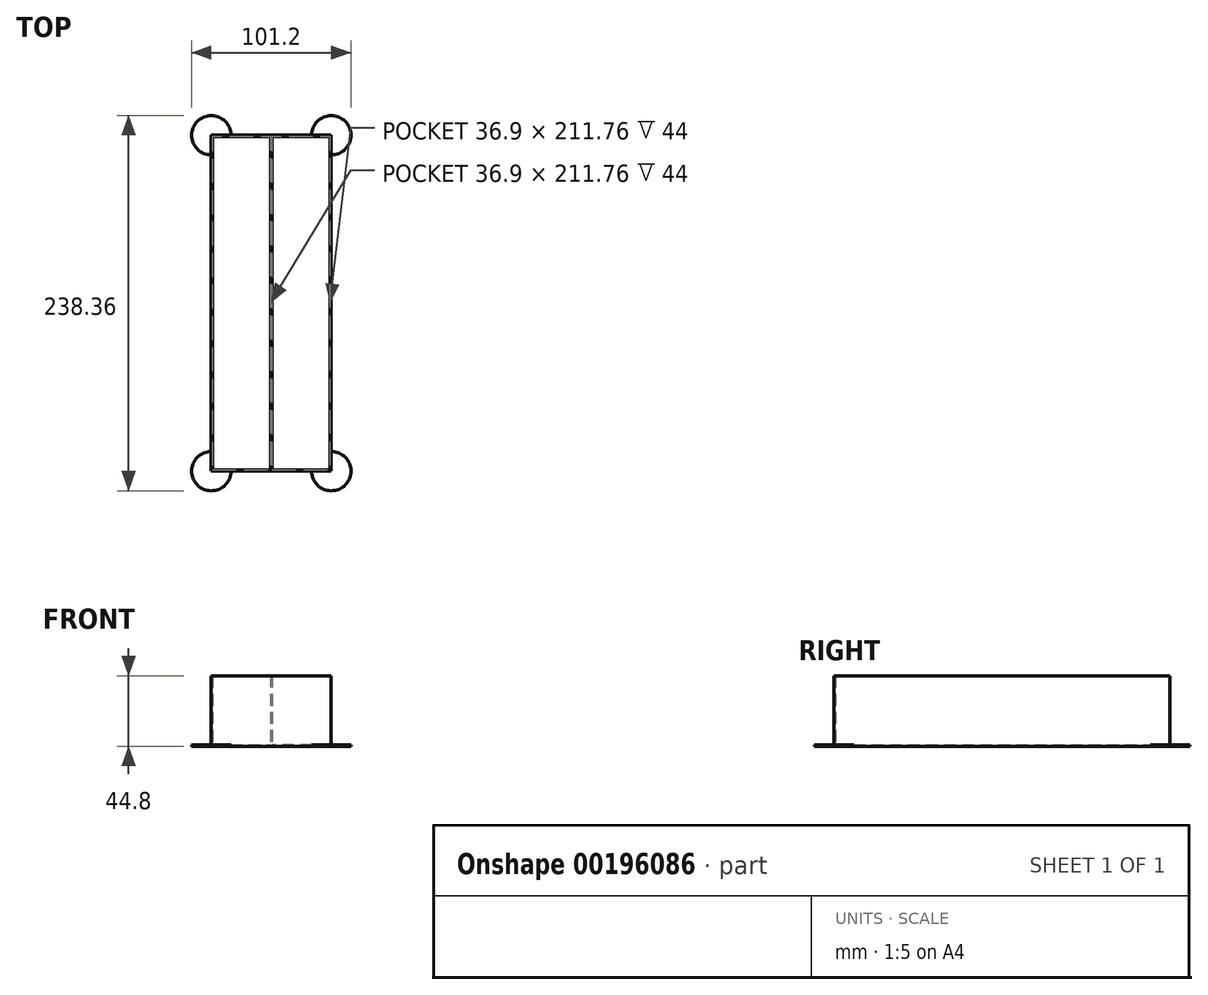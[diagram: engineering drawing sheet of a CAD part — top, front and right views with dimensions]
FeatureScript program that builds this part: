
annotation { "Feature Type Name" : "Feature", "Feature Type Description" : "" }
export const myFeature = defineFeature(function(context is Context, id is Id, definition is map)
    precondition{}
    {
        {
            var Q0;
            Q0=qCreatedBy(makeId("Top.planeOp"),FACE);
            var sketch = newSketch(context, id + "F0", { "sketchPlane" : qUnion([Q0])});
            skLineSegment(sketch, "E0.bottom", {"start": v(0, 0) * mm, "end": v(76.2, 0) * mm});
            skLineSegment(sketch, "E0.top", {"start": v(0, 213.36) * mm, "end": v(76.2, 213.36) * mm});
            skLineSegment(sketch, "E0.left", {"start": v(0, 0) * mm, "end": v(0, 213.36) * mm});
            skLineSegment(sketch, "E0.right", {"start": v(76.2, 0) * mm, "end": v(76.2, 213.36) * mm});
            skCircle(sketch, "E1", {"center": v(76.2, 0) * mm, "radius": 12.5 * mm});
            skCircle(sketch, "E2", {"center": v(0, 0) * mm, "radius": 12.5 * mm});
            skCircle(sketch, "E3", {"center": v(76.2, 213.36) * mm, "radius": 12.5 * mm});
            skCircle(sketch, "E4", {"center": v(0, 213.36) * mm, "radius": 12.5 * mm});
            skSolve(sketch);
        }
        {
            var Q0;
            Q0=makeQuery(id+"F0.imprint","IMPRINT",FACE,{"disambiguationData":[TD([[makeQuery(id+"F0.imprint","IMPRINT",EDGE,{"derivedFrom":sQuery(id+"F0.wireOp",EDGE,"E0.bottom")}),1.0]])]});
            var Q1;
            {var subQ5=sQuery(id+"F0.wireOp",EDGE,"E2");var subQ10=sQuery(id+"F0.wireOp",EDGE,"E0.bottom");var subQ11=makeQuery(id+"F0.imprint","INTERSECT",VERTEX,{"derivedFrom":[subQ10,subQ5]});Q1=makeQuery(id+"F0.imprint","IMPRINT",FACE,{"disambiguationData":[TD([[makeQuery(id+"F0.imprint","IMPRINT",EDGE,{"disambiguationData":[TD([[subQ11,-1.0]])],"derivedFrom":subQ10}),1.0]])]});}
            var Q2;
            {var subQ0=sQuery(id+"F0.wireOp",EDGE,"E0.right");var subQ1=sQuery(id+"F0.wireOp",EDGE,"E0.top");var subQ2=makeQuery(id+"F0.imprint","INTERSECT",VERTEX,{"derivedFrom":[subQ1,subQ0]});Q2=makeQuery(id+"F0.imprint","IMPRINT",FACE,{"disambiguationData":[TD([[makeQuery(id+"F0.imprint","IMPRINT",EDGE,{"disambiguationData":[TD([[subQ2,1.0]])],"derivedFrom":subQ1}),-1.0]])]});}
            var Q3;
            {var subQ0=sQuery(id+"F0.wireOp",EDGE,"E0.left");var subQ1=sQuery(id+"F0.wireOp",EDGE,"E0.top");var subQ2=makeQuery(id+"F0.imprint","INTERSECT",VERTEX,{"derivedFrom":[subQ1,subQ0]});Q3=makeQuery(id+"F0.imprint","IMPRINT",FACE,{"disambiguationData":[TD([[makeQuery(id+"F0.imprint","IMPRINT",EDGE,{"disambiguationData":[TD([[subQ2,-1.0]])],"derivedFrom":subQ1}),-1.0]])]});}
            extrude(context, id + "F1", {"entities" : qUnion([Q0, Q1, Q2, Q3]), "depth" : 0.8 * mm});
        }
        {
            var Q0;
            Q0=makeQuery(id+"F1.opExtrude","CAP_FACE",FACE,{"disambiguationData":[OSD([sQuery(id+"F0.wireOp",EDGE,"E0.bottom"),sQuery(id+"F0.wireOp",EDGE,"E0.top"),sQuery(id+"F0.wireOp",EDGE,"E0.left"),sQuery(id+"F0.wireOp",EDGE,"E0.right")])],"isStart":false});
            var sketch = newSketch(context, id + "F2", { "sketchPlane" : qUnion([Q0])});
            skLineSegment(sketch, "E5.0", {"start": v(0, 213.36) * mm, "end": v(76.2, 213.36) * mm});
            skLineSegment(sketch, "E5.1", {"start": v(0, 0) * mm, "end": v(0, 213.36) * mm});
            skLineSegment(sketch, "E5.2", {"start": v(76.2, 0) * mm, "end": v(76.2, 213.36) * mm});
            skLineSegment(sketch, "E5.3", {"start": v(0, 0) * mm, "end": v(76.2, 0) * mm});
            skLineSegment(sketch, "E6", {"start": v(38.1, 213.36) * mm, "end": v(38.1, 0) * mm, "construction": true});
            skLineSegment(sketch, "E7.bottom", {"start": v(0.8, 212.56) * mm, "end": v(37.7, 212.56) * mm});
            skLineSegment(sketch, "E7.top", {"start": v(0.8, 0.8) * mm, "end": v(37.7, 0.8) * mm});
            skLineSegment(sketch, "E7.left", {"start": v(0.8, 212.56) * mm, "end": v(0.8, 0.8) * mm});
            skLineSegment(sketch, "E7.right", {"start": v(37.7, 212.56) * mm, "end": v(37.7, 0.8) * mm});
            skLineSegment(sketch, "E8.bottom", {"start": v(75.4, 0.8) * mm, "end": v(38.5, 0.8) * mm});
            skLineSegment(sketch, "E8.top", {"start": v(75.4, 212.56) * mm, "end": v(38.5, 212.56) * mm});
            skLineSegment(sketch, "E8.left", {"start": v(75.4, 0.8) * mm, "end": v(75.4, 212.56) * mm});
            skLineSegment(sketch, "E8.right", {"start": v(38.5, 0.8) * mm, "end": v(38.5, 212.56) * mm});
            skSolve(sketch);
        }
        {
            var Q0;
            Q0 = qSketchRegion(id + "F2", true);
            extrude(context, id + "F3", {"entities" : qUnion([Q0]), "operationType" : NewBodyOperationType.ADD, "depth" : 44 * mm});
        }
        {
            var Q0;
            {var subQ0=sQuery(id+"F0.wireOp",EDGE,"E0.right");var subQ1=sQuery(id+"F0.wireOp",EDGE,"E0.bottom");var subQ2=makeQuery(id+"F0.imprint","INTERSECT",VERTEX,{"derivedFrom":[subQ1,subQ0]});Q0=makeQuery(id+"F0.imprint","IMPRINT",FACE,{"disambiguationData":[TD([[makeQuery(id+"F0.imprint","IMPRINT",EDGE,{"disambiguationData":[TD([[subQ2,1.0]])],"derivedFrom":subQ1}),-1.0]])]});}
            var Q1;
            {var subQ0=sQuery(id+"F0.wireOp",EDGE,"E0.left");var subQ1=sQuery(id+"F0.wireOp",EDGE,"E0.bottom");var subQ2=makeQuery(id+"F0.imprint","INTERSECT",VERTEX,{"derivedFrom":[subQ1,subQ0]});Q1=makeQuery(id+"F0.imprint","IMPRINT",FACE,{"disambiguationData":[TD([[makeQuery(id+"F0.imprint","IMPRINT",EDGE,{"disambiguationData":[TD([[subQ2,-1.0]])],"derivedFrom":subQ1}),-1.0]])]});}
            var Q2;
            {var subQ0=sQuery(id+"F0.wireOp",EDGE,"E0.left");var subQ1=sQuery(id+"F0.wireOp",EDGE,"E0.top");var subQ2=makeQuery(id+"F0.imprint","INTERSECT",VERTEX,{"derivedFrom":[subQ1,subQ0]});Q2=makeQuery(id+"F0.imprint","IMPRINT",FACE,{"disambiguationData":[TD([[makeQuery(id+"F0.imprint","IMPRINT",EDGE,{"disambiguationData":[TD([[subQ2,-1.0]])],"derivedFrom":subQ1}),1.0]])]});}
            var Q3;
            {var subQ0=sQuery(id+"F0.wireOp",EDGE,"E0.right");var subQ1=sQuery(id+"F0.wireOp",EDGE,"E0.top");var subQ2=makeQuery(id+"F0.imprint","INTERSECT",VERTEX,{"derivedFrom":[subQ1,subQ0]});Q3=makeQuery(id+"F0.imprint","IMPRINT",FACE,{"disambiguationData":[TD([[makeQuery(id+"F0.imprint","IMPRINT",EDGE,{"disambiguationData":[TD([[subQ2,1.0]])],"derivedFrom":subQ1}),1.0]])]});}
            var Q4;
            {var subQ0=sQuery(id+"F0.wireOp",EDGE,"E0.right");var subQ1=sQuery(id+"F0.wireOp",EDGE,"E0.bottom");var subQ2=makeQuery(id+"F0.imprint","INTERSECT",VERTEX,{"derivedFrom":[subQ1,subQ0]});Q4=makeQuery(id+"F0.imprint","IMPRINT",FACE,{"disambiguationData":[TD([[makeQuery(id+"F0.imprint","IMPRINT",EDGE,{"disambiguationData":[TD([[subQ2,1.0]])],"derivedFrom":subQ1}),1.0]])]});}
            var Q5;
            {var subQ0=sQuery(id+"F0.wireOp",EDGE,"E0.left");var subQ1=sQuery(id+"F0.wireOp",EDGE,"E0.bottom");var subQ2=makeQuery(id+"F0.imprint","INTERSECT",VERTEX,{"derivedFrom":[subQ1,subQ0]});Q5=makeQuery(id+"F0.imprint","IMPRINT",FACE,{"disambiguationData":[TD([[makeQuery(id+"F0.imprint","IMPRINT",EDGE,{"disambiguationData":[TD([[subQ2,-1.0]])],"derivedFrom":subQ1}),1.0]])]});}
            var Q6;
            {var subQ0=sQuery(id+"F0.wireOp",EDGE,"E0.left");var subQ1=sQuery(id+"F0.wireOp",EDGE,"E0.top");var subQ2=makeQuery(id+"F0.imprint","INTERSECT",VERTEX,{"derivedFrom":[subQ1,subQ0]});Q6=makeQuery(id+"F0.imprint","IMPRINT",FACE,{"disambiguationData":[TD([[makeQuery(id+"F0.imprint","IMPRINT",EDGE,{"disambiguationData":[TD([[subQ2,-1.0]])],"derivedFrom":subQ1}),-1.0]])]});}
            var Q7;
            {var subQ0=sQuery(id+"F0.wireOp",EDGE,"E0.right");var subQ1=sQuery(id+"F0.wireOp",EDGE,"E0.top");var subQ2=makeQuery(id+"F0.imprint","INTERSECT",VERTEX,{"derivedFrom":[subQ1,subQ0]});Q7=makeQuery(id+"F0.imprint","IMPRINT",FACE,{"disambiguationData":[TD([[makeQuery(id+"F0.imprint","IMPRINT",EDGE,{"disambiguationData":[TD([[subQ2,1.0]])],"derivedFrom":subQ1}),-1.0]])]});}
            var Q8;
            Q8=makeQuery(id+"FiQekbZnkU5w3n6_1.boolean.opBoolean","SPLIT",FACE,{"disambiguationData":[TD([makeQuery(id+"FiQekbZnkU5w3n6_1.opExtrude","SWEPT_FACE",FACE,{"disambiguationData":[OSD([sQuery(id+"FYhHQeHNSpe778E_1.wireOp",EDGE,"fp9y7PvB-vgqv-VAFc-78NA-D35dIFwHA4oR.top")])]})])],"derivedFrom":makeQuery(id+"F1.opExtrude","CAP_FACE",FACE,{"disambiguationData":[OSD([sQuery(id+"F0.wireOp",EDGE,"E0.bottom"),sQuery(id+"F0.wireOp",EDGE,"E0.top"),sQuery(id+"F0.wireOp",EDGE,"E0.left"),sQuery(id+"F0.wireOp",EDGE,"E0.right")])],"isStart":false})});
            extrude(context, id + "F4", {"entities" : qUnion([Q0, Q1, Q2, Q3, Q4, Q5, Q6, Q7]), "operationType" : NewBodyOperationType.ADD, "endBound" : BoundingType.UP_TO_SURFACE, "endBoundEntityFace" : qUnion([Q8]), "depth" : 25 * mm});
        }
    });
